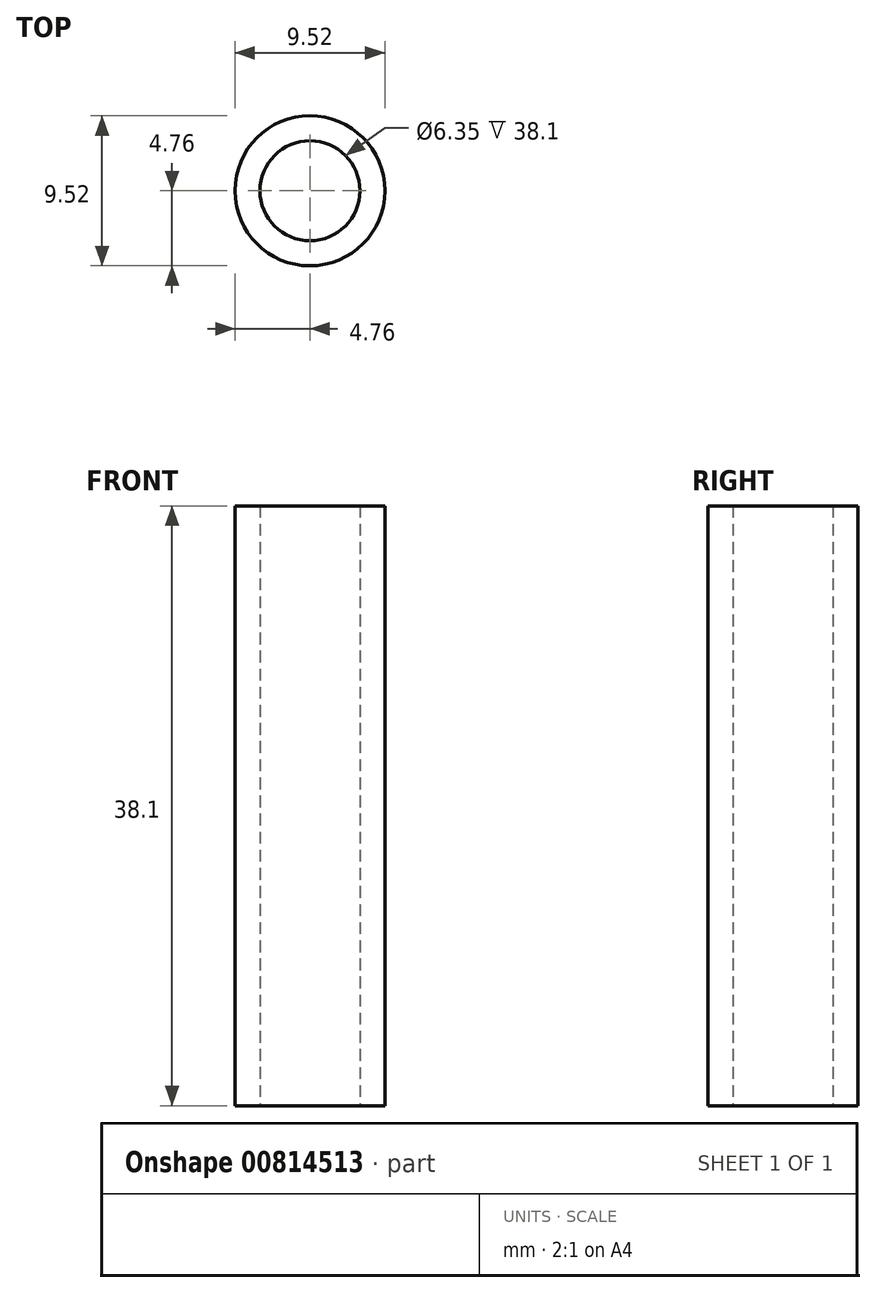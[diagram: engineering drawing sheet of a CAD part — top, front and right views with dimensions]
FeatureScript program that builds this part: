
annotation { "Feature Type Name" : "Feature", "Feature Type Description" : "" }
export const myFeature = defineFeature(function(context is Context, id is Id, definition is map)
    precondition{}
    {
        {
            var Q0;
            Q0=qCreatedBy(makeId("Top.planeOp"),FACE);
            var sketch = newSketch(context, id + "F0", { "sketchPlane" : qUnion([Q0])});
            skCircle(sketch, "E0", {"center": v(0, 0) * mm, "radius": 4.76 * mm});
            skCircle(sketch, "E1", {"center": v(0, 0) * mm, "radius": 3.18 * mm});
            skSolve(sketch);
        }
        {
            var Q0;
            Q0=makeQuery(id+"F0.imprint","IMPRINT",FACE,{"disambiguationData":[TD([[makeQuery(id+"F0.imprint","IMPRINT",EDGE,{"derivedFrom":sQuery(id+"F0.wireOp",EDGE,"E0")}),1.0]])]});
            extrude(context, id + "F1", {"entities" : qUnion([Q0]), "depth" : 38.1 * mm, "offsetDistance" : 25.4 * mm});
        }
    });
